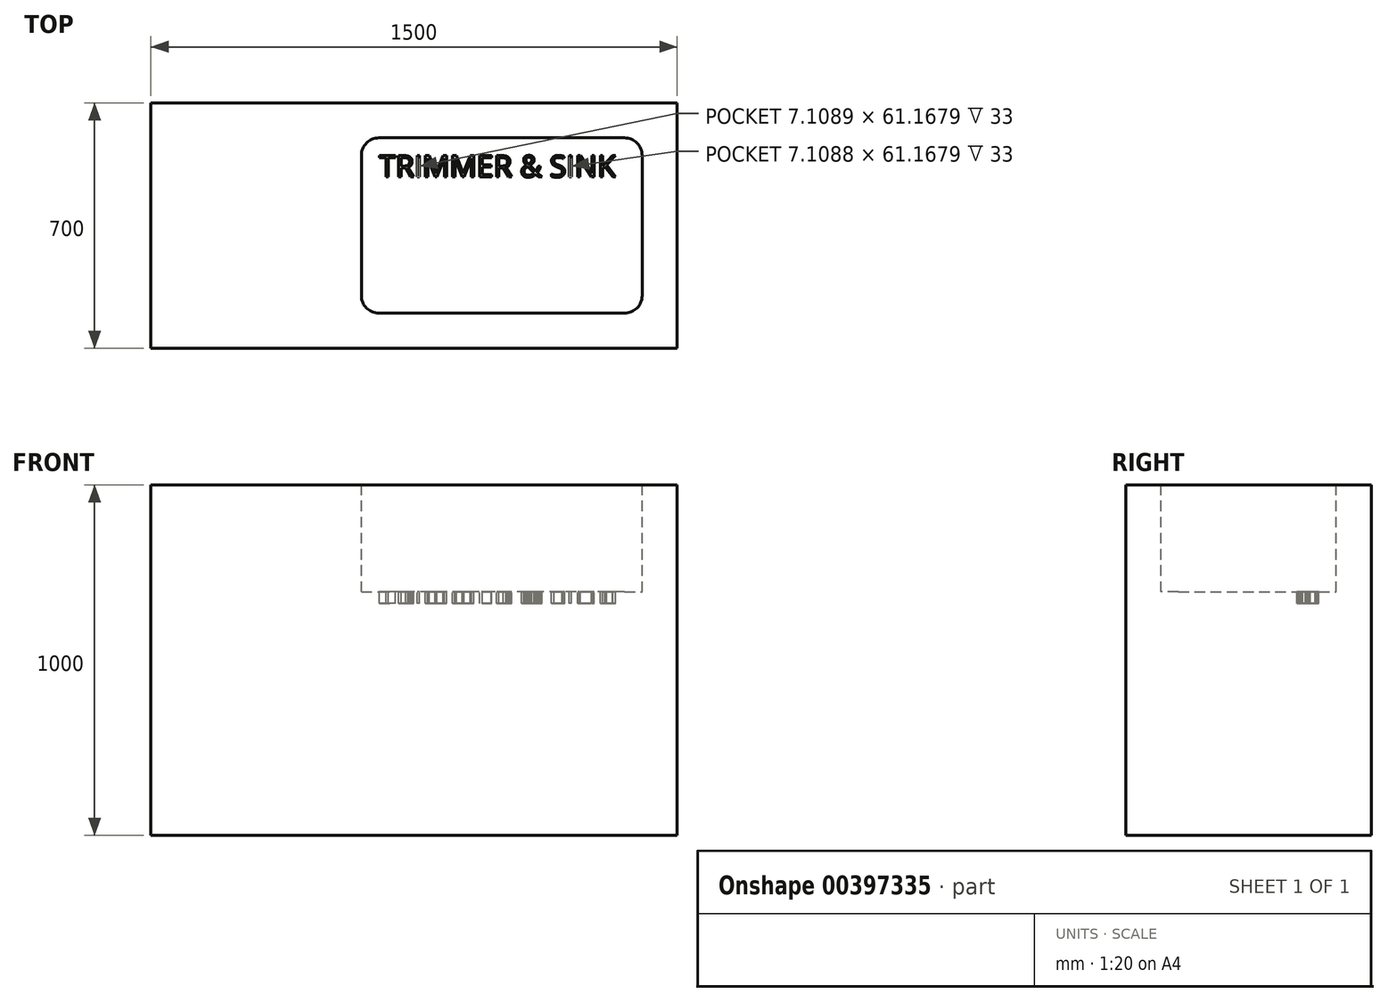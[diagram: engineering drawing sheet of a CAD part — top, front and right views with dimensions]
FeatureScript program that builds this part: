
annotation { "Feature Type Name" : "Feature", "Feature Type Description" : "" }
export const myFeature = defineFeature(function(context is Context, id is Id, definition is map)
    precondition{}
    {
        {
            var Q0;
            Q0=qCreatedBy(makeId("Top.planeOp"),FACE);
            var sketch = newSketch(context, id + "F0", { "sketchPlane" : qUnion([Q0])});
            skLineSegment(sketch, "E0.bottom", {"start": v(750, -350) * mm, "end": v(-750, -350) * mm});
            skLineSegment(sketch, "E0.top", {"start": v(750, 350) * mm, "end": v(-750, 350) * mm});
            skLineSegment(sketch, "E0.left", {"start": v(750, -350) * mm, "end": v(750, 350) * mm});
            skLineSegment(sketch, "E0.right", {"start": v(-750, -350) * mm, "end": v(-750, 350) * mm});
            skPoint(sketch, "E0.middle", {"position": v(0, 0) * mm});
            skSolve(sketch);
        }
        {
            var Q0;
            Q0 = qSketchRegion(id + "F0", true);
            extrude(context, id + "F1", {"entities" : qUnion([Q0]), "depth" : 1000 * mm});
        }
        {
            var Q0;
            Q0=makeQuery(id+"F1.opExtrude","CAP_FACE",FACE,{"disambiguationData":[OSD([sQuery(id+"F0.wireOp",EDGE,"E0.bottom"),sQuery(id+"F0.wireOp",EDGE,"E0.top"),sQuery(id+"F0.wireOp",EDGE,"E0.left"),sQuery(id+"F0.wireOp",EDGE,"E0.right")])],"isStart":false});
            var sketch = newSketch(context, id + "F2", { "sketchPlane" : qUnion([Q0])});
            skLineSegment(sketch, "E1.bottom", {"start": v(600, -250) * mm, "end": v(-100, -250) * mm});
            skLineSegment(sketch, "E1.top", {"start": v(600, 250) * mm, "end": v(-100, 250) * mm});
            skLineSegment(sketch, "E1.left", {"start": v(650, -200) * mm, "end": v(650, 200) * mm});
            skLineSegment(sketch, "E1.right", {"start": v(-150, -200) * mm, "end": v(-150, 200) * mm});
            skPoint(sketch, "E1.middle", {"position": v(250, 0) * mm});
            skPoint(sketch, "E2.visualSharp", {"position": v(-150, 250) * mm});
            skArc(sketch, "E2.filletArc", {"start": v(-150, 245.04) * mm, "mid": v(-150, 245.04) * mm, "end": v(-150, 245.04) * mm});
            skArc(sketch, "E3.filletArc", {"start": v(-100, 250) * mm, "mid": v(-135.36, 235.36) * mm, "end": v(-150, 200) * mm});
            skPoint(sketch, "E4.visualSharp", {"position": v(-150, -250) * mm});
            skArc(sketch, "E4.filletArc", {"start": v(-150, -200) * mm, "mid": v(-135.36, -235.36) * mm, "end": v(-100, -250) * mm});
            skPoint(sketch, "E5.visualSharp", {"position": v(650, -250) * mm});
            skArc(sketch, "E5.filletArc", {"start": v(600, -250) * mm, "mid": v(635.36, -235.36) * mm, "end": v(650, -200) * mm});
            skPoint(sketch, "E6.visualSharp", {"position": v(650, 250) * mm});
            skArc(sketch, "E6.filletArc", {"start": v(650, 200) * mm, "mid": v(635.36, 235.36) * mm, "end": v(600, 250) * mm});
            skSolve(sketch);
        }
        {
            var Q0;
            Q0 = qSketchRegion(id + "F2", true);
            extrude(context, id + "F3", {"entities" : qUnion([Q0]), "operationType" : NewBodyOperationType.REMOVE, "oppositeDirection" : true, "depth" : 305 * mm});
        }
        {
            var Q0;
            Q0=makeQuery(id+"F3.boolean.opBoolean","COPY",FACE,{"derivedFrom":makeQuery(id+"F3.opExtrude","CAP_FACE",FACE,{"disambiguationData":[OSD([sQuery(id+"F2.wireOp",EDGE,"E1.bottom"),sQuery(id+"F2.wireOp",EDGE,"E1.top"),sQuery(id+"F2.wireOp",EDGE,"E1.left"),sQuery(id+"F2.wireOp",EDGE,"E1.right"),sQuery(id+"F2.wireOp",EDGE,"E3.filletArc"),sQuery(id+"F2.wireOp",EDGE,"E4.filletArc"),sQuery(id+"F2.wireOp",EDGE,"E5.filletArc"),sQuery(id+"F2.wireOp",EDGE,"E6.filletArc")])],"isStart":false})});
            var sketch = newSketch(context, id + "F4", { "sketchPlane" : qUnion([Q0])});
            skText(sketch, "E7", { "text": "TRIMMER & SINK", "fontName": "OpenSans-Regular.ttf"});
            const initialGuessF4  = {"E7": [-0.1, 0.13831, 1, 0, 0.06169]};
            skSetInitialGuess(sketch, initialGuessF4);
            skSolve(sketch);
        }
        {
            var Q0;
            Q0 = qSketchRegion(id + "F4", true);
            extrude(context, id + "F5", {"entities" : qUnion([Q0]), "operationType" : NewBodyOperationType.REMOVE, "oppositeDirection" : true, "depth" : 33 * mm});
        }
    });
